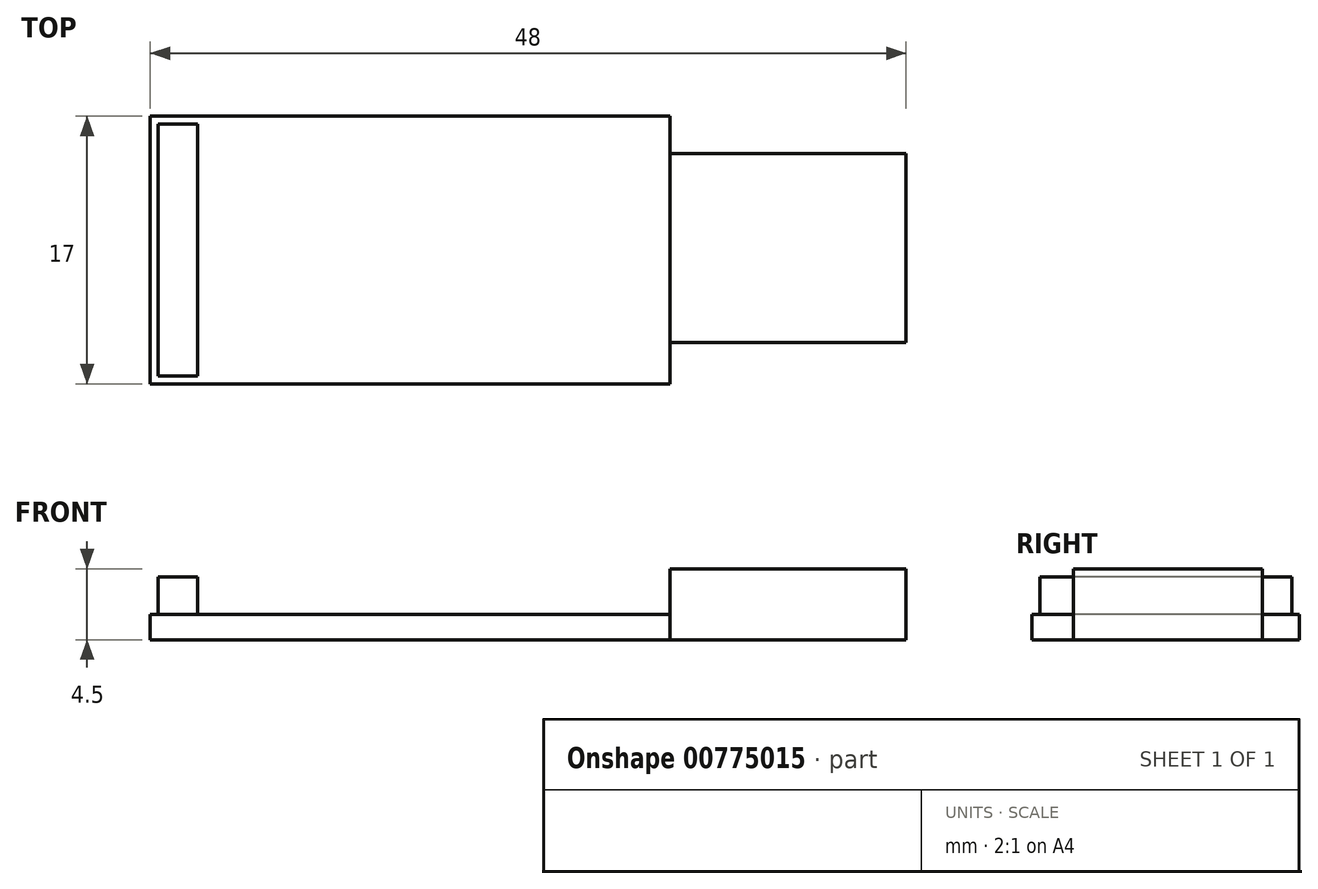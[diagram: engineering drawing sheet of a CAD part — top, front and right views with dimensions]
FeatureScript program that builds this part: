
annotation { "Feature Type Name" : "Feature", "Feature Type Description" : "" }
export const myFeature = defineFeature(function(context is Context, id is Id, definition is map)
    precondition{}
    {
        {
            var Q0;
            Q0=qCreatedBy(makeId("Top.planeOp"),FACE);
            var sketch = newSketch(context, id + "F0", { "sketchPlane" : qUnion([Q0])});
            skLineSegment(sketch, "E0.bottom", {"start": v(-48, -0.57) * mm, "end": v(-15, -0.57) * mm});
            skLineSegment(sketch, "E0.top", {"start": v(-48, -17.57) * mm, "end": v(-15, -17.57) * mm});
            skLineSegment(sketch, "E0.left", {"start": v(-48, -0.57) * mm, "end": v(-48, -17.57) * mm});
            skLineSegment(sketch, "E0.right", {"start": v(-15, -0.57) * mm, "end": v(-15, -17.57) * mm});
            skLineSegment(sketch, "E1.bottom", {"start": v(-15, -2.94) * mm, "end": v(0, -2.94) * mm});
            skLineSegment(sketch, "E1.top", {"start": v(-15, -14.94) * mm, "end": v(0, -14.94) * mm});
            skLineSegment(sketch, "E1.left", {"start": v(-15, -2.94) * mm, "end": v(-15, -14.94) * mm});
            skLineSegment(sketch, "E1.right", {"start": v(0, -2.94) * mm, "end": v(0, -14.94) * mm});
            skSolve(sketch);
        }
        {
            var Q0;
            {var subQ1=sQuery(id+"F0.wireOp",EDGE,"E0.bottom");Q0=makeQuery(id+"F0.imprint","IMPRINT",FACE,{"disambiguationData":[TD([[makeQuery(id+"F0.imprint","IMPRINT",EDGE,{"derivedFrom":subQ1}),-1.0]])]});}
            extrude(context, id + "F1", {"entities" : qUnion([Q0]), "depth" : 1.6 * mm, "offsetDistance" : 25 * mm});
        }
        {
            var Q0;
            Q0=makeQuery(id+"F0.imprint","IMPRINT",FACE,{"disambiguationData":[TD([[makeQuery(id+"F0.imprint","IMPRINT",EDGE,{"derivedFrom":sQuery(id+"F0.wireOp",EDGE,"E1.bottom")}),-1.0]])]});
            extrude(context, id + "F2", {"entities" : qUnion([Q0]), "operationType" : NewBodyOperationType.ADD, "depth" : 4.5 * mm, "offsetDistance" : 25 * mm});
        }
        {
            var Q0;
            Q0=makeQuery(id+"F1.opExtrude","CAP_FACE",FACE,{"disambiguationData":[OSD([sQuery(id+"F0.wireOp",EDGE,"E0.bottom"),sQuery(id+"F0.wireOp",EDGE,"E0.top"),sQuery(id+"F0.wireOp",EDGE,"E0.left"),sQuery(id+"F0.wireOp",EDGE,"E0.right"),sQuery(id+"F0.wireOp",EDGE,"E1.left")])],"isStart":false});
            var sketch = newSketch(context, id + "F3", { "sketchPlane" : qUnion([Q0])});
            skLineSegment(sketch, "E2.bottom", {"start": v(-45, -1.06) * mm, "end": v(-47.5, -1.06) * mm});
            skLineSegment(sketch, "E2.top", {"start": v(-45, -17.06) * mm, "end": v(-47.5, -17.06) * mm});
            skLineSegment(sketch, "E2.left", {"start": v(-45, -1.06) * mm, "end": v(-45, -17.06) * mm});
            skLineSegment(sketch, "E2.right", {"start": v(-47.5, -1.06) * mm, "end": v(-47.5, -17.06) * mm});
            skSolve(sketch);
        }
        {
            var Q0;
            Q0=makeQuery(id+"F3.imprint","IMPRINT",FACE,{"disambiguationData":[TD([[makeQuery(id+"F3.imprint","IMPRINT",EDGE,{"derivedFrom":sQuery(id+"F3.wireOp",EDGE,"E2.bottom")}),1.0]])]});
            extrude(context, id + "F4", {"entities" : qUnion([Q0]), "operationType" : NewBodyOperationType.ADD, "depth" : 2.4 * mm, "offsetDistance" : 25 * mm});
        }
    });
